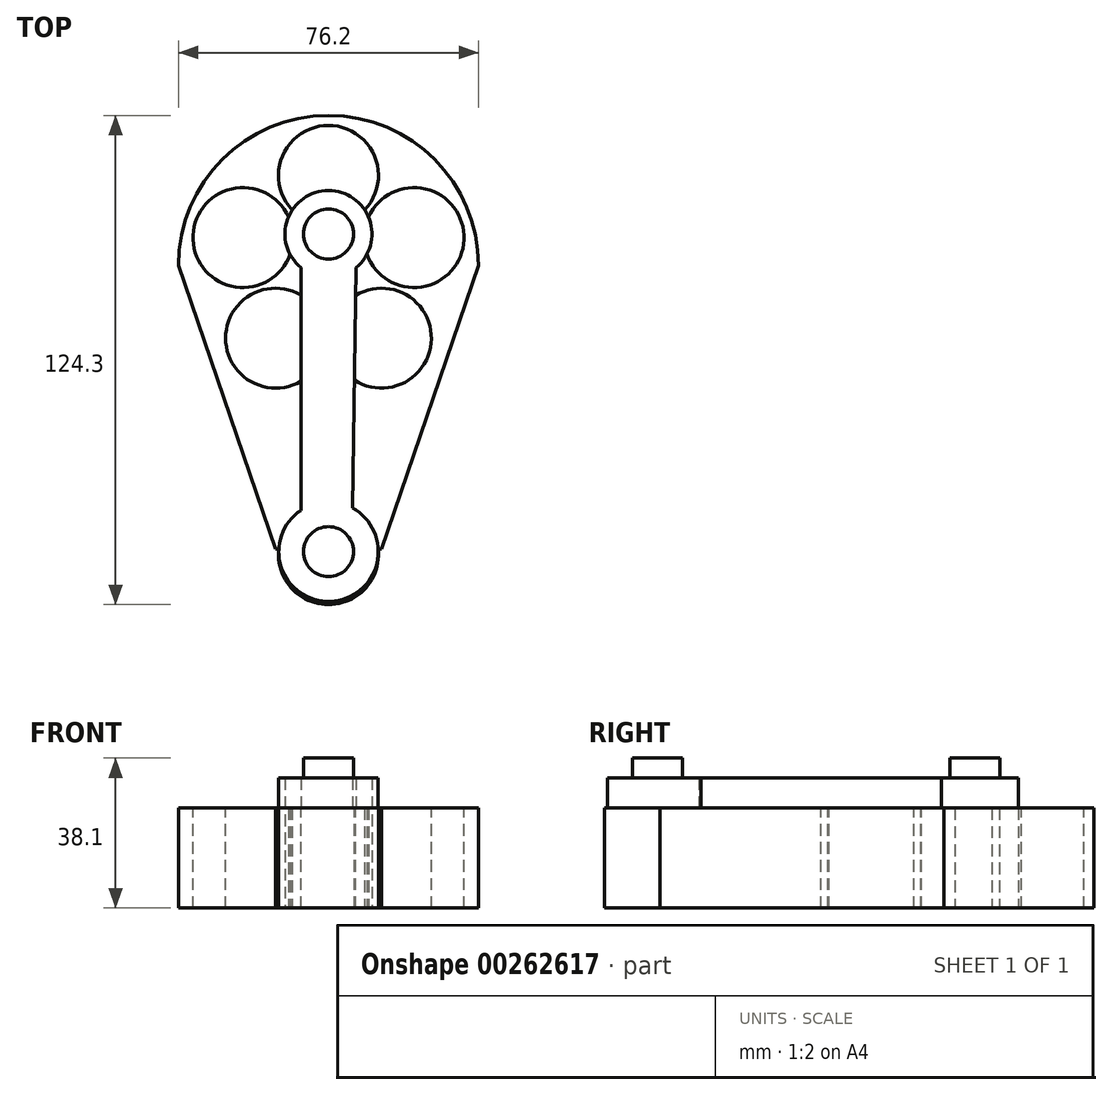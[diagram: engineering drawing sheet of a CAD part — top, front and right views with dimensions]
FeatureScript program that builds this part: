
annotation { "Feature Type Name" : "Feature", "Feature Type Description" : "" }
export const myFeature = defineFeature(function(context is Context, id is Id, definition is map)
    precondition{}
    {
        {
            var Q0;
            Q0=qCreatedBy(makeId("Top.planeOp"),FACE);
            var sketch = newSketch(context, id + "F0", { "sketchPlane" : qUnion([Q0])});
            skArc(sketch, "E0", {"start": v(38.1, 0) * mm, "mid": v(0, 38.1) * mm, "end": v(-38.1, 0) * mm});
            skLineSegment(sketch, "E1", {"start": v(-38.1, 0) * mm, "end": v(-13.42, -72.1) * mm});
            skLineSegment(sketch, "E2", {"start": v(38.1, 0) * mm, "end": v(13.42, -72.1) * mm});
            skLineSegment(sketch, "E3", {"start": v(-13.42, -72.1) * mm, "end": v(-12.7, -72.1) * mm});
            skLineSegment(sketch, "E4.trimOffspring", {"start": v(12.7, -72.1) * mm, "end": v(13.42, -72.1) * mm});
            skArc(sketch, "E5", {"start": v(-12.62, -72.1) * mm, "mid": v(0, -86.2) * mm, "end": v(12.62, -72.1) * mm});
            skLineSegment(sketch, "E6", {"start": v(-12.7, -72.1) * mm, "end": v(-12.62, -72.1) * mm});
            skLineSegment(sketch, "E7.trimOffspring", {"start": v(12.62, -72.1) * mm, "end": v(13.42, -72.1) * mm});
            skSolve(sketch);
        }
        {
            var Q0;
            Q0 = qSketchRegion(id + "F0", true);
            extrude(context, id + "F1", {"entities" : qUnion([Q0]), "depth" : 25.4 * mm});
        }
        {
            var Q0;
            Q0=makeQuery(id+"F1.opExtrude","CAP_FACE",FACE,{"disambiguationData":[OSD([sQuery(id+"F0.wireOp",EDGE,"E0"),sQuery(id+"F0.wireOp",EDGE,"E1"),sQuery(id+"F0.wireOp",EDGE,"E2"),sQuery(id+"F0.wireOp",EDGE,"E3"),sQuery(id+"F0.wireOp",EDGE,"E5"),sQuery(id+"F0.wireOp",EDGE,"E6"),sQuery(id+"F0.wireOp",EDGE,"E7.trimOffspring")])],"isStart":false});
            var sketch = newSketch(context, id + "F2", { "sketchPlane" : qUnion([Q0])});
            skCircle(sketch, "E8", {"center": v(0, 22.86) * mm, "radius": 12.7 * mm});
            skSolve(sketch);
        }
        {
            var Q0;
            Q0=makeQuery(id+"F2.imprint","IMPRINT",FACE,{"disambiguationData":[TD([[makeQuery(id+"F2.imprint","IMPRINT",EDGE,{"derivedFrom":sQuery(id+"F2.wireOp",EDGE,"E8")}),1.0]])]});
            extrude(context, id + "F3", {"entities" : qUnion([Q0]), "operationType" : NewBodyOperationType.REMOVE, "oppositeDirection" : true, "depth" : 25.4 * mm});
        }
        {
            var Q0;
            Q0=makeQuery(id+"F1.opExtrude","CAP_FACE",FACE,{"disambiguationData":[OSD([sQuery(id+"F0.wireOp",EDGE,"E0"),sQuery(id+"F0.wireOp",EDGE,"E1"),sQuery(id+"F0.wireOp",EDGE,"E2"),sQuery(id+"F0.wireOp",EDGE,"E3"),sQuery(id+"F0.wireOp",EDGE,"E5"),sQuery(id+"F0.wireOp",EDGE,"E6"),sQuery(id+"F0.wireOp",EDGE,"E7.trimOffspring")])],"isStart":false});
            var sketch = newSketch(context, id + "F4", { "sketchPlane" : qUnion([Q0])});
            skCircle(sketch, "E9.0", {"center": v(0, 22.86) * mm, "radius": 12.7 * mm});
            skCircle(sketch, "E10.1.0", {"center": v(-21.74, 7.06) * mm, "radius": 12.7 * mm});
            skCircle(sketch, "E10.2.0", {"center": v(-13.44, -18.5) * mm, "radius": 12.7 * mm});
            skCircle(sketch, "E10.3.0", {"center": v(13.44, -18.5) * mm, "radius": 12.7 * mm});
            skCircle(sketch, "E10.4.0", {"center": v(21.74, 7.06) * mm, "radius": 12.7 * mm});
            skPoint(sketch, "E10.center", {"position": v(0, 0) * mm});
            skSolve(sketch);
        }
        {
            var Q0;
            Q0=makeQuery(id+"F4.imprint","IMPRINT",FACE,{"disambiguationData":[TD([[makeQuery(id+"F4.imprint","IMPRINT",EDGE,{"derivedFrom":sQuery(id+"F4.wireOp",EDGE,"E10.1.0")}),1.0]])]});
            extrude(context, id + "F5", {"entities" : qUnion([Q0]), "operationType" : NewBodyOperationType.REMOVE, "oppositeDirection" : true, "depth" : 25.4 * mm});
        }
        {
            var Q0;
            Q0 = qSketchRegion(id + "F4", true);
            extrude(context, id + "F6", {"entities" : qUnion([Q0]), "operationType" : NewBodyOperationType.REMOVE, "oppositeDirection" : true, "depth" : 25.4 * mm});
        }
        {
            var Q0;
            Q0=qCreatedBy(makeId("Top.planeOp"),FACE);
            var sketch = newSketch(context, id + "F7", { "sketchPlane" : qUnion([Q0])});
            skArc(sketch, "E11.0", {"start": v(38.1, 0) * mm, "mid": v(0, 38.1) * mm, "end": v(-38.1, 0) * mm});
            skLineSegment(sketch, "E12.0", {"start": v(-38.1, 0) * mm, "end": v(-13.42, -72.1) * mm});
            skPoint(sketch, "E13.0", {"position": v(0, -86.2) * mm});
            skLineSegment(sketch, "E14.0", {"start": v(38.1, 0) * mm, "end": v(13.42, -72.1) * mm});
            skLineSegment(sketch, "E15", {"start": v(-7.01, -62.22) * mm, "end": v(-7.01, 0) * mm});
            skLineSegment(sketch, "E16.MirrorCS", {"start": v(6.1, -61.67) * mm, "end": v(7.01, 0) * mm});
            skArc(sketch, "E17", {"start": v(7, -0.57) * mm, "mid": v(0, 19.03) * mm, "end": v(-7.01, -0.56) * mm});
            skPoint(sketch, "E18.start.orphan", {"position": v(0, 38.1) * mm});
            skPoint(sketch, "E19.orphan", {"position": v(12.62, -72.1) * mm});
            skPoint(sketch, "E20.0.start.orphan", {"position": v(-12.62, -72.1) * mm});
            skArc(sketch, "E21", {"start": v(-7.01, -62.22) * mm, "mid": v(0.53, -85.36) * mm, "end": v(6.1, -61.67) * mm});
            skSolve(sketch);
        }
        {
            var Q0;
            Q0 = qSketchRegion(id + "F7", true);
            extrude(context, id + "F8", {"entities" : qUnion([Q0]), "operationType" : NewBodyOperationType.ADD, "depth" : 33.02 * mm});
        }
        {
            var Q0;
            Q0=makeQuery(id+"F8.opExtrude","CAP_FACE",FACE,{"disambiguationData":[OSD([sQuery(id+"F7.wireOp",EDGE,"E15"),sQuery(id+"F7.wireOp",EDGE,"E16.MirrorCS"),sQuery(id+"F7.wireOp",EDGE,"E17"),sQuery(id+"F7.wireOp",EDGE,"E21")])],"isStart":false});
            var sketch = newSketch(context, id + "F9", { "sketchPlane" : qUnion([Q0])});
            skCircle(sketch, "E22", {"center": v(0, 7.98) * mm, "radius": 6.35 * mm});
            skCircle(sketch, "E23", {"center": v(0, -72.74) * mm, "radius": 6.35 * mm});
            skSolve(sketch);
        }
        {
            var Q0;
            Q0 = qSketchRegion(id + "F9", true);
            extrude(context, id + "F10", {"entities" : qUnion([Q0]), "operationType" : NewBodyOperationType.ADD, "depth" : 5.08 * mm});
        }
    });
